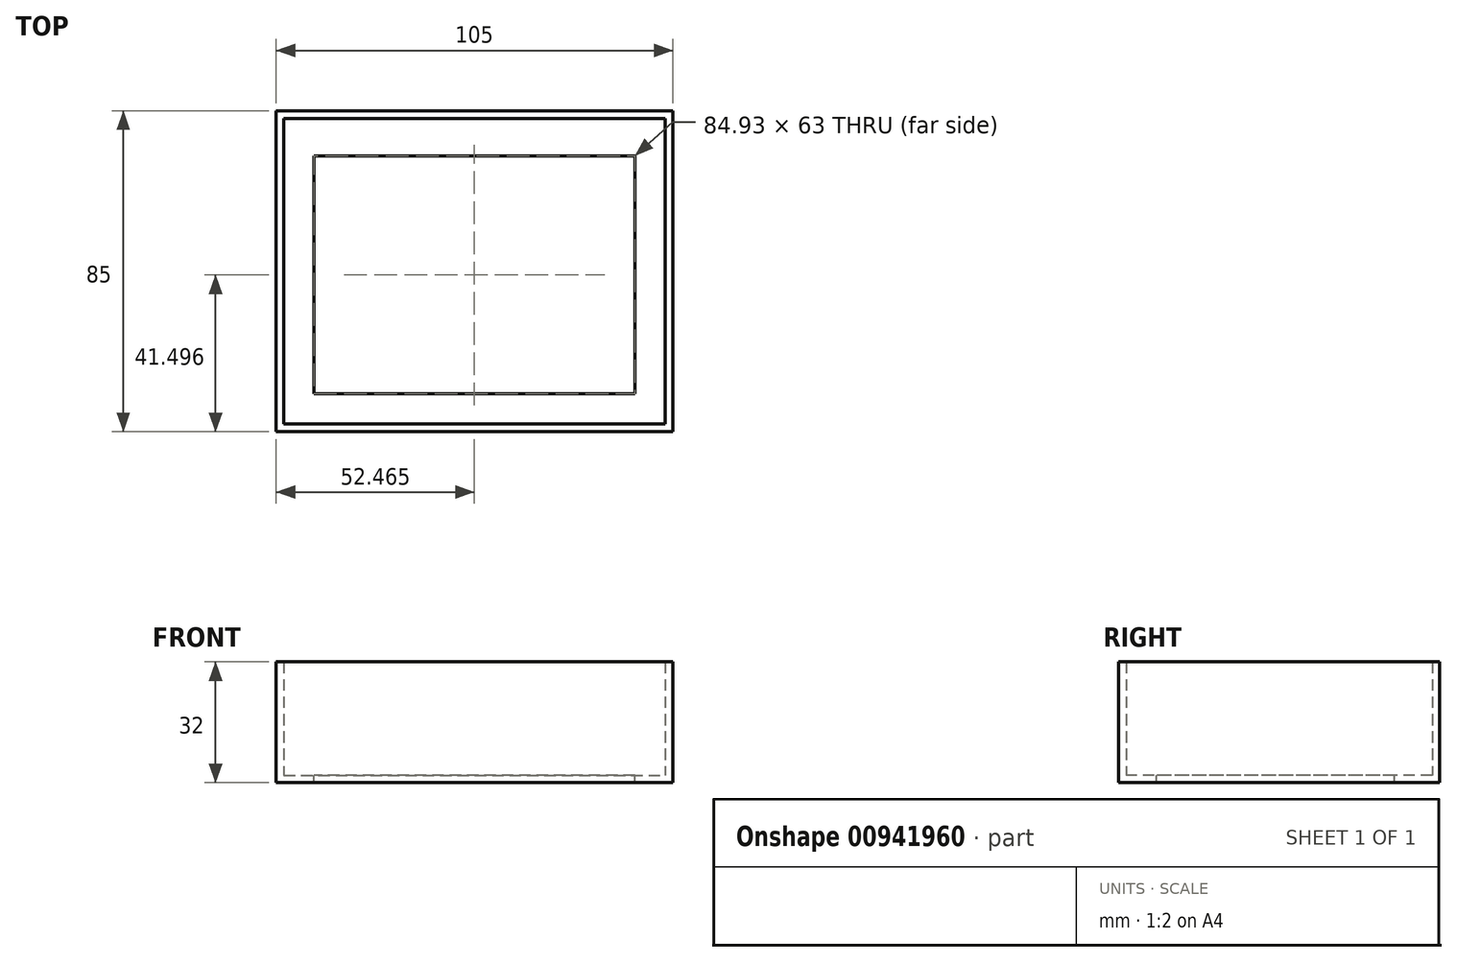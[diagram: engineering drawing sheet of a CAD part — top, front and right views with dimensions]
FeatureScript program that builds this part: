
annotation { "Feature Type Name" : "Feature", "Feature Type Description" : "" }
export const myFeature = defineFeature(function(context is Context, id is Id, definition is map)
    precondition{}
    {
        {
            var Q0;
            Q0=qCreatedBy(makeId("Top.planeOp"),FACE);
            var sketch = newSketch(context, id + "F0", { "sketchPlane" : qUnion([Q0])});
            skLineSegment(sketch, "E0.bottom", {"start": v(-48.53, 42.47) * mm, "end": v(56.47, 42.47) * mm});
            skLineSegment(sketch, "E0.top", {"start": v(-48.53, -42.53) * mm, "end": v(56.47, -42.53) * mm});
            skLineSegment(sketch, "E0.left", {"start": v(-48.53, 42.47) * mm, "end": v(-48.53, -42.53) * mm});
            skLineSegment(sketch, "E0.right", {"start": v(56.47, 42.47) * mm, "end": v(56.47, -42.53) * mm});
            skLineSegment(sketch, "E1", {"start": v(-46.53, 11.64) * mm, "end": v(-46.53, 40.47) * mm});
            skLineSegment(sketch, "E2", {"start": v(-46.53, 40.47) * mm, "end": v(54.47, 40.47) * mm});
            skLineSegment(sketch, "E3", {"start": v(54.47, 40.47) * mm, "end": v(54.47, -40.53) * mm});
            skLineSegment(sketch, "E4", {"start": v(54.47, -40.53) * mm, "end": v(-46.53, -40.53) * mm});
            skLineSegment(sketch, "E5", {"start": v(-46.53, 11.64) * mm, "end": v(-46.53, -40.53) * mm});
            skPoint(sketch, "E6.orphan", {"position": v(-46.53, 42.47) * mm});
            skSolve(sketch);
        }
        {
            var Q0;
            Q0=makeQuery(id+"F0.imprint","IMPRINT",FACE,{"disambiguationData":[TD([[makeQuery(id+"F0.imprint","IMPRINT",EDGE,{"derivedFrom":sQuery(id+"F0.wireOp",EDGE,"E0.bottom")}),-1.0]])]});
            extrude(context, id + "F1", {"entities" : qUnion([Q0]), "depth" : 30 * mm, "offsetDistance" : 25 * mm});
        }
        {
            var Q0;
            Q0=makeQuery(id+"F1.opExtrude","CAP_FACE",FACE,{"disambiguationData":[OSD([sQuery(id+"F0.wireOp",EDGE,"E0.bottom"),sQuery(id+"F0.wireOp",EDGE,"E0.top"),sQuery(id+"F0.wireOp",EDGE,"E0.left"),sQuery(id+"F0.wireOp",EDGE,"E0.right"),sQuery(id+"F0.wireOp",EDGE,"E1"),sQuery(id+"F0.wireOp",EDGE,"E2"),sQuery(id+"F0.wireOp",EDGE,"E3"),sQuery(id+"F0.wireOp",EDGE,"E4"),sQuery(id+"F0.wireOp",EDGE,"E5")])],"isStart":true});
            var sketch = newSketch(context, id + "F2", { "sketchPlane" : qUnion([Q0])});
            skLineSegment(sketch, "E7.bottom", {"start": v(-48.53, 42.53) * mm, "end": v(56.47, 42.53) * mm});
            skLineSegment(sketch, "E7.top", {"start": v(-48.53, -42.47) * mm, "end": v(56.47, -42.47) * mm});
            skLineSegment(sketch, "E7.left", {"start": v(-48.53, 42.53) * mm, "end": v(-48.53, -42.47) * mm});
            skLineSegment(sketch, "E7.right", {"start": v(56.47, 42.53) * mm, "end": v(56.47, -42.47) * mm});
            skLineSegment(sketch, "E8", {"start": v(-48.53, 42.53) * mm, "end": v(-38.53, 42.53) * mm});
            skLineSegment(sketch, "E9", {"start": v(-38.53, 32.53) * mm, "end": v(46.4, 32.53) * mm});
            skLineSegment(sketch, "E10", {"start": v(46.4, 32.53) * mm, "end": v(46.4, -30.47) * mm});
            skLineSegment(sketch, "E11", {"start": v(46.4, -30.47) * mm, "end": v(-38.53, -30.47) * mm});
            skLineSegment(sketch, "E12", {"start": v(-38.53, -30.47) * mm, "end": v(-38.53, 32.53) * mm});
            skPoint(sketch, "E13.start.orphan", {"position": v(56.47, 32.53) * mm});
            skSolve(sketch);
        }
        {
            var Q0;
            Q0 = qSketchRegion(id + "F2", true);
            extrude(context, id + "F3", {"entities" : qUnion([Q0]), "operationType" : NewBodyOperationType.ADD, "depth" : 2 * mm, "offsetDistance" : 25 * mm});
        }
    });
